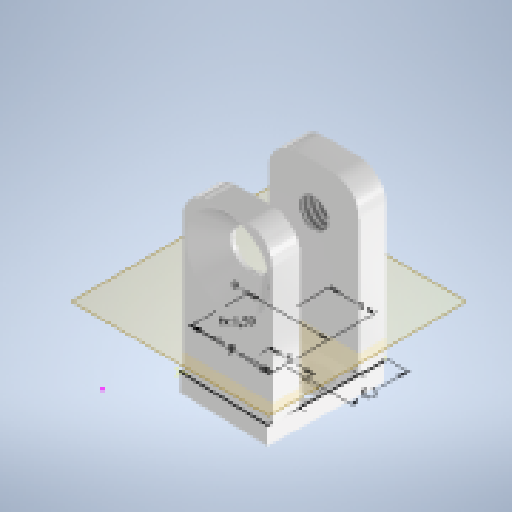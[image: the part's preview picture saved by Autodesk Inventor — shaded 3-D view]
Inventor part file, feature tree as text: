
AUTODESK INVENTOR PART (.ipt)
format: ipt  version: 2025 (Build 290162010, 162A)  size: 239,104 bytes
history: native  units: mm
features: sketch x4, hole x3, extrude x2, fillet x1, plane x1
ambient origin geometry x8: Origin, YZ Plane, XZ Plane, XY Plane, X Axis, Y Axis, Z Axis, Center Point
bodies: Volumenkörper1 (feature_tree)
feature tree (11):
  extrude  "Extrusion1"  Depth=3.0mm
  fillet  "Rundung1"  Radius=3.0mm
  hole  "Bohrung1"  [1 undecoded]
  plane  "Arbeitsebene1"
  sketch  "Skizze4"  dims[d7=3.0mm]
  extrude  "Extrusion3"  Depth=2.0mm
  hole  "Bohrung2"  [1 undecoded]
  hole  "Bohrung3"  [1 undecoded]
  sketch  "Skizze1"  dims[d0=10.0mm d1=3.0mm d2=3.0mm]
  sketch  "Skizze2"  dims[d3=6.6mm d5=18.0mm d6=0.0mm]
  sketch  "Skizze5"  dims[d8=4.3mm d9=8.0mm d10=9.4mm d11=14.0mm d12=90.0deg d13=11.8mm d14=20.594885mm d19=2.0mm d20=8.0mm d21=5.0mm d22=2.0mm d23=90.0deg d24=8.0mm d25=20.594885mm d26=3.242mm d27=8.0mm d28=4.0mm d29=2.0mm d30=90.0deg d31=5.0mm d32=20.594885mm d34=5.0mm d35=9.0mm d36=6.3mm d37=5.0mm d38=9.0mm d40=9.0mm d41=0.277101mm d42=2.0mm d43=0.0mm]
note: 3 required parameter values undecoded (feature->parameter linkage not recoverable at this tier; creation-order binding heuristic only, values carry confidence <= 0.55)
